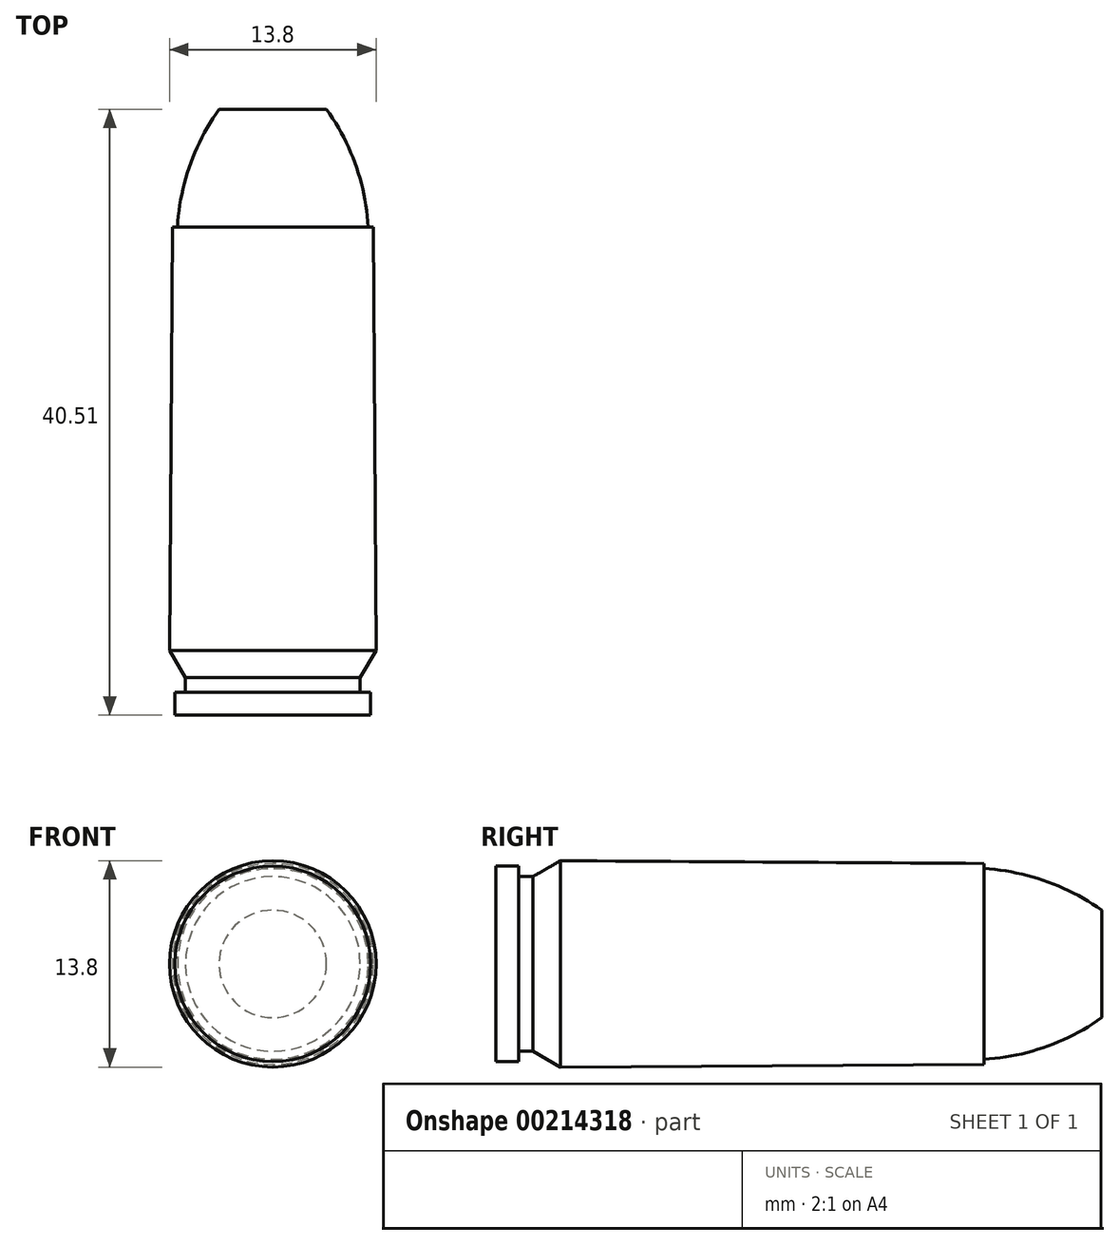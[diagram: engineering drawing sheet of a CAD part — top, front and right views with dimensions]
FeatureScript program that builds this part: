
annotation { "Feature Type Name" : "Feature", "Feature Type Description" : "" }
export const myFeature = defineFeature(function(context is Context, id is Id, definition is map)
    precondition{}
    {
        {
            var Q0;
            Q0=qCreatedBy(makeId("Right.planeOp"),FACE);
            var sketch = newSketch(context, id + "F0", { "sketchPlane" : qUnion([Q0])});
            skLineSegment(sketch, "E0", {"start": v(0, 0) * mm, "end": v(0, 6.54) * mm});
            skLineSegment(sketch, "E1", {"start": v(0, 6.54) * mm, "end": v(1.52, 6.54) * mm});
            skLineSegment(sketch, "E2", {"start": v(1.52, 6.54) * mm, "end": v(1.52, 5.84) * mm});
            skLineSegment(sketch, "E3", {"start": v(1.52, 5.84) * mm, "end": v(2.49, 5.84) * mm});
            skLineSegment(sketch, "E4", {"start": v(36.78, 0) * mm, "end": v(0, 0) * mm});
            skLineSegment(sketch, "E5", {"start": v(4.32, 6.9) * mm, "end": v(32.64, 6.72) * mm});
            skLineSegment(sketch, "E6", {"start": v(32.64, 6.72) * mm, "end": v(32.64, 0) * mm});
            skLineSegment(sketch, "E7", {"start": v(2.49, 5.84) * mm, "end": v(4.32, 6.9) * mm});
            skLineSegment(sketch, "E8", {"start": v(5.08, 6.9) * mm, "end": v(5.08, 0) * mm});
            skSolve(sketch);
        }
        {
            var Q0;
            Q0 = qSketchRegion(id + "F0", true);
            var Q1;
            Q1=sQuery(id+"F0.wireOp",EDGE,"E4");
            revolve(context, id + "F1", {"entities" : qUnion([Q0]), "axis" : qUnion([Q1]), "revolveType" : RevolveType.FULL});
        }
        {
            var Q0;
            Q0=qCreatedBy(makeId("Right.planeOp"),FACE);
            var sketch = newSketch(context, id + "F2", { "sketchPlane" : qUnion([Q0])});
            skLineSegment(sketch, "E9.0", {"start": v(32.64, 6.72) * mm, "end": v(32.64, -6.72) * mm});
            skLineSegment(sketch, "E10", {"start": v(40.51, 3.6) * mm, "end": v(40.51, 0) * mm});
            skLineSegment(sketch, "E11", {"start": v(40.51, 0) * mm, "end": v(32.64, 0) * mm});
            skArc(sketch, "E12", {"start": v(40.51, 3.6) * mm, "mid": v(36.77, 5.55) * mm, "end": v(32.64, 6.38) * mm});
            skSolve(sketch);
        }
        {
            var Q0;
            Q0=makeQuery(id+"F2.imprint","IMPRINT",FACE,{"disambiguationData":[TD([[makeQuery(id+"F2.imprint","IMPRINT",EDGE,{"derivedFrom":sQuery(id+"F2.wireOp",EDGE,"E10")}),-1.0]])]});
            var Q1;
            Q1=sQuery(id+"F2.wireOp",EDGE,"E11");
            revolve(context, id + "F3", {"operationType" : NewBodyOperationType.ADD, "entities" : qUnion([Q0]), "axis" : qUnion([Q1]), "revolveType" : RevolveType.FULL});
        }
    });
